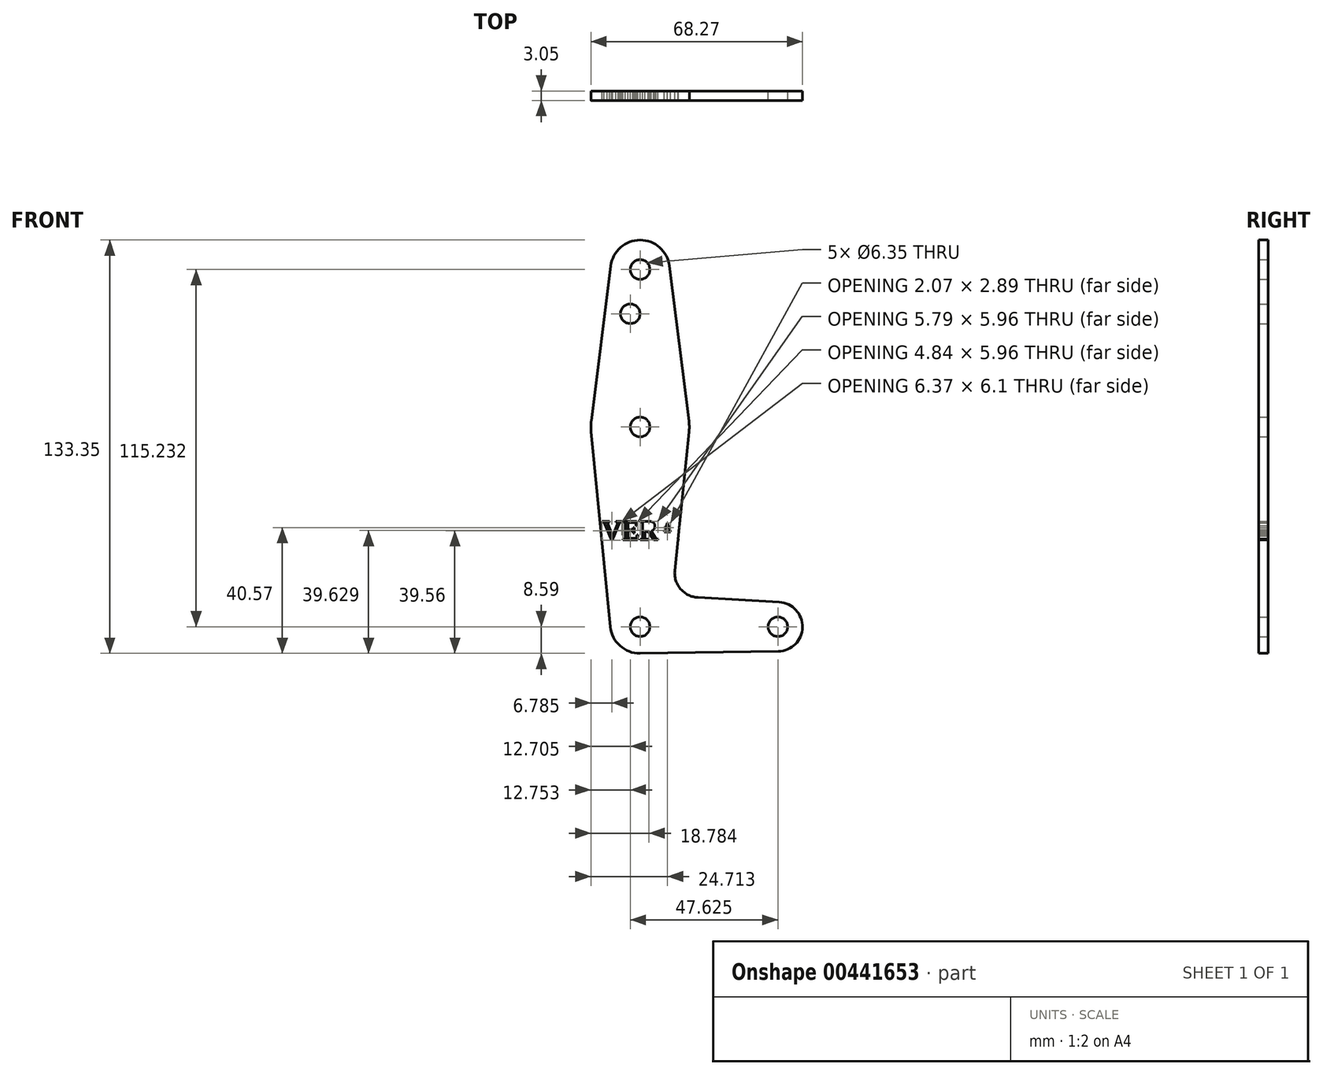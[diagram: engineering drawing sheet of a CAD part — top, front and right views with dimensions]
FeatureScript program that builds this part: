
annotation { "Feature Type Name" : "Feature", "Feature Type Description" : "" }
export const myFeature = defineFeature(function(context is Context, id is Id, definition is map)
    precondition{}
    {
        {
            var Q0;
            Q0=qCreatedBy(makeId("Front.planeOp"),FACE);
            var sketch = newSketch(context, id + "F0", { "sketchPlane" : qUnion([Q0])});
            skLineSegment(sketch, "E0", {"start": v(0, 115.23) * mm, "end": v(0, 0) * mm, "construction": true});
            skLineSegment(sketch, "E1", {"start": v(0, 0) * mm, "end": v(44.45, 0) * mm, "construction": true});
            skCircle(sketch, "E2", {"center": v(0, 115.23) * mm, "radius": 9.53 * mm});
            skCircle(sketch, "E3", {"center": v(0, 64.43) * mm, "radius": 15.88 * mm});
            skCircle(sketch, "E4", {"center": v(-0.14, 0.93) * mm, "radius": 9.53 * mm});
            skCircle(sketch, "E5", {"center": v(44.45, 0) * mm, "radius": 7.94 * mm});
            skLineSegment(sketch, "E6", {"start": v(18.66, 9.4) * mm, "end": v(44.9, 7.92) * mm});
            skLineSegment(sketch, "E7", {"start": v(0, -8.6) * mm, "end": v(44.9, -7.93) * mm});
            skLineSegment(sketch, "E8", {"start": v(-9.62, 0) * mm, "end": v(-15.8, 62.88) * mm});
            skLineSegment(sketch, "E9", {"start": v(11.2, 18.16) * mm, "end": v(15.8, 62.8) * mm});
            skLineSegment(sketch, "E10", {"start": v(-9.45, 116.42) * mm, "end": v(-15.75, 66.42) * mm});
            skLineSegment(sketch, "E11", {"start": v(9.45, 116.42) * mm, "end": v(15.75, 66.42) * mm});
            skCircle(sketch, "E12", {"center": v(0, 115.23) * mm, "radius": 3.18 * mm});
            skCircle(sketch, "E13", {"center": v(0, 64.43) * mm, "radius": 3.18 * mm});
            skCircle(sketch, "E14", {"center": v(0, 0) * mm, "radius": 3.18 * mm});
            skCircle(sketch, "E15", {"center": v(44.45, 0) * mm, "radius": 3.18 * mm});
            skCircle(sketch, "E16", {"center": v(-3.17, 100.96) * mm, "radius": 3.18 * mm});
            skArc(sketch, "E17.filletArc", {"start": v(11.2, 18.16) * mm, "mid": v(13.06, 12.19) * mm, "end": v(18.66, 9.4) * mm});
            skText(sketch, "E18", { "text": "VERA", "fontName": "Tinos-Regular.ttf"});
            const initialGuessF0  = {"E18": [-0.01238, 0.02806, 1, 0, 0.00655]};
            skSetInitialGuess(sketch, initialGuessF0);
            skSolve(sketch);
        }
        {
            var Q0;
            Q0 = qSketchRegion(id + "F0", true);
            extrude(context, id + "F1", {"entities" : qUnion([Q0]), "depth" : 3.05 * mm});
        }
    });
